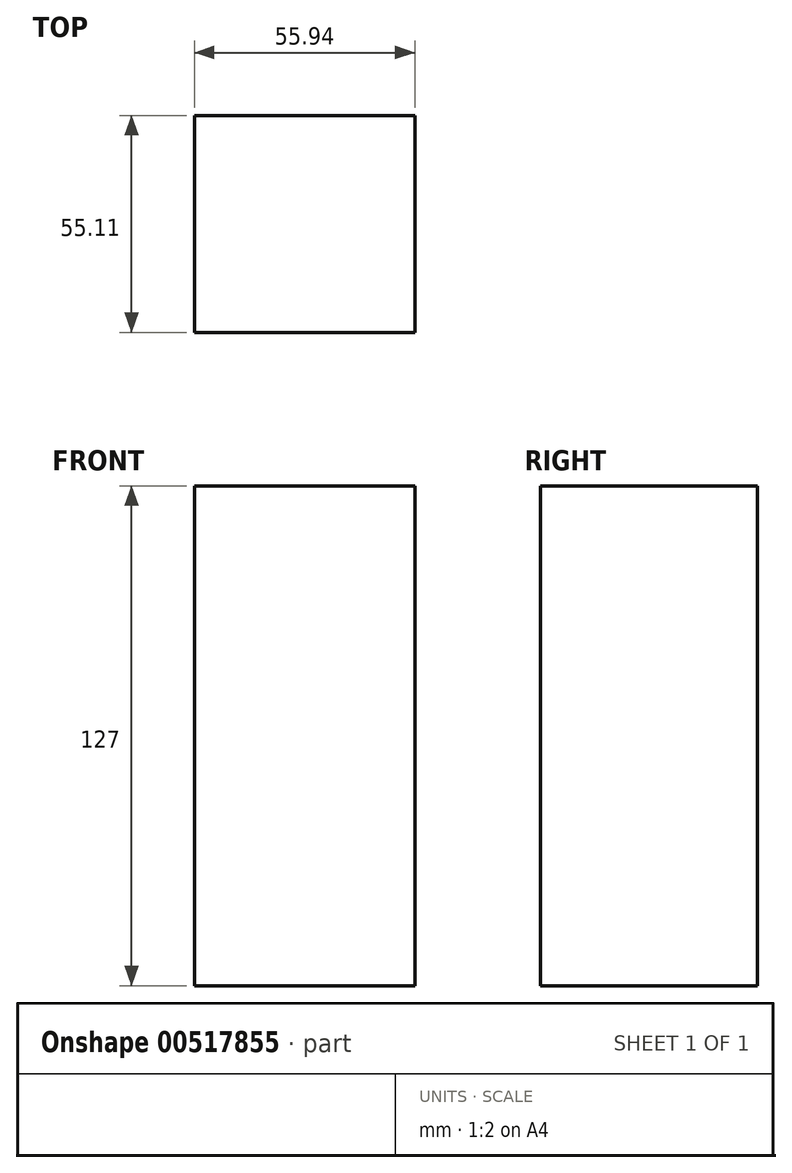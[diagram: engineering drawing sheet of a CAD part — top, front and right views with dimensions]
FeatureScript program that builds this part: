
annotation { "Feature Type Name" : "Feature", "Feature Type Description" : "" }
export const myFeature = defineFeature(function(context is Context, id is Id, definition is map)
    precondition{}
    {
        {
            var Q0;
            Q0=qCreatedBy(makeId("Top.planeOp"),FACE);
            var sketch = newSketch(context, id + "F0", { "sketchPlane" : qUnion([Q0])});
            skLineSegment(sketch, "E0.bottom", {"start": v(-76.94, -75.28) * mm, "end": v(-21, -75.28) * mm});
            skLineSegment(sketch, "E0.top", {"start": v(-76.94, -20.17) * mm, "end": v(-21, -20.17) * mm});
            skLineSegment(sketch, "E0.left", {"start": v(-76.94, -75.28) * mm, "end": v(-76.94, -20.17) * mm});
            skLineSegment(sketch, "E0.right", {"start": v(-21, -75.28) * mm, "end": v(-21, -20.17) * mm});
            skSolve(sketch);
        }
        {
            var Q0;
            Q0 = qSketchRegion(id + "F0", true);
            extrude(context, id + "F1", {"entities" : qUnion([Q0]), "depth" : 127 * mm, "offsetDistance" : 25.4 * mm});
        }
    });
